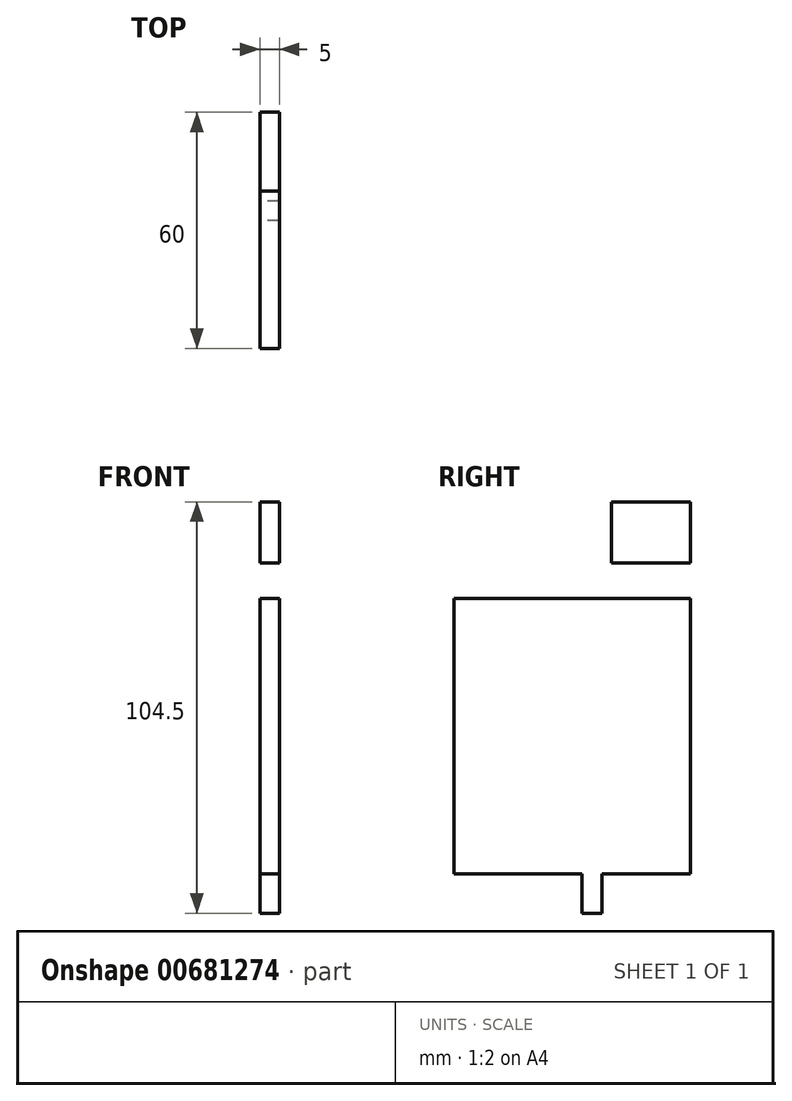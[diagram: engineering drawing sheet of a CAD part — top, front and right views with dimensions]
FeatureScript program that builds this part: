
annotation { "Feature Type Name" : "Feature", "Feature Type Description" : "" }
export const myFeature = defineFeature(function(context is Context, id is Id, definition is map)
    precondition{}
    {
        {
            var Q0;
            Q0=qCreatedBy(makeId("Right.planeOp"),FACE);
            var sketch = newSketch(context, id + "F0", { "sketchPlane" : qUnion([Q0])});
            skLineSegment(sketch, "E0", {"start": v(0, 0) * mm, "end": v(0, -70) * mm});
            skLineSegment(sketch, "E1", {"start": v(0, -70) * mm, "end": v(12.4, -70) * mm});
            skLineSegment(sketch, "E2.0", {"start": v(37.5, -70.04) * mm, "end": v(37.5, -81.07) * mm});
            skLineSegment(sketch, "E3", {"start": v(12, -70) * mm, "end": v(12.4, -70) * mm});
            skLineSegment(sketch, "E4", {"start": v(0, -70) * mm, "end": v(12, -70) * mm});
            skLineSegment(sketch, "E5", {"start": v(32.5, -80) * mm, "end": v(32.5, -70) * mm});
            skPoint(sketch, "E6.trimOffspring.start.orphan", {"position": v(25, -70) * mm});
            skLineSegment(sketch, "E7", {"start": v(37.5, -80) * mm, "end": v(37.5, -81.07) * mm});
            skLineSegment(sketch, "E8", {"start": v(32.5, -80) * mm, "end": v(37.5, -80) * mm});
            skLineSegment(sketch, "E9", {"start": v(11.37, -27.14) * mm, "end": v(11.37, -26.74) * mm});
            skLineSegment(sketch, "E10", {"start": v(38.63, -27.14) * mm, "end": v(38.63, -26.74) * mm});
            skLineSegment(sketch, "E11", {"start": v(0, -70) * mm, "end": v(32.5, -70) * mm});
            skLineSegment(sketch, "E12.trimOffspring", {"start": v(32.5, -70) * mm, "end": v(0, -70) * mm});
            skLineSegment(sketch, "E13", {"start": v(22.5, -0.04) * mm, "end": v(0, 0) * mm});
            skLineSegment(sketch, "E14.0", {"start": v(60, -0.04) * mm, "end": v(60, -70.04) * mm});
            skLineSegment(sketch, "E15", {"start": v(60, -0.04) * mm, "end": v(22.5, -0.04) * mm});
            skLineSegment(sketch, "E16", {"start": v(60, -70.04) * mm, "end": v(37.5, -70.04) * mm});
            skLineSegment(sketch, "E17.0", {"start": v(42.5, 9) * mm, "end": v(40, 9) * mm});
            skPoint(sketch, "E18.orphan", {"position": v(42.5, 0) * mm});
            skLineSegment(sketch, "E19", {"start": v(40, 24.5) * mm, "end": v(42.5, 24.5) * mm});
            skPoint(sketch, "E19.startSnap0", {"position": v(42.5, 24.5) * mm});
            skPoint(sketch, "E19.endSnap0", {"position": v(42.5, 24.5) * mm});
            skPoint(sketch, "E20.end.orphan", {"position": v(42.5, 40) * mm});
            skLineSegment(sketch, "E21", {"start": v(60, 9) * mm, "end": v(60, 24.5) * mm});
            skLineSegment(sketch, "E22", {"start": v(42.5, 24.5) * mm, "end": v(60, 24.5) * mm});
            skLineSegment(sketch, "E23", {"start": v(42.5, 9) * mm, "end": v(60, 9) * mm});
            skPoint(sketch, "E24.orphan", {"position": v(22.5, 24.5) * mm});
            skLineSegment(sketch, "E25.0", {"start": v(40, 9) * mm, "end": v(40, 24.5) * mm});
            skSolve(sketch);
        }
        {
            var Q0;
            {var subQ1=sQuery(id+"F0.wireOp",EDGE,"E0");Q0=makeQuery(id+"F0.imprint","IMPRINT",FACE,{"disambiguationData":[TD([[makeQuery(id+"F0.imprint","IMPRINT",EDGE,{"derivedFrom":subQ1}),1.0]])]});}
            var Q1;
            Q1=makeQuery(id+"F0.imprint","IMPRINT",FACE,{"disambiguationData":[TD([[makeQuery(id+"F0.imprint","IMPRINT",EDGE,{"derivedFrom":sQuery(id+"F0.wireOp",EDGE,"KUJi0EKv-68yc-6Nkf-644W-VpfIH1upkmh2")}),-1.0]])]});
            var Q2;
            Q2=makeQuery(id+"F0.imprint","IMPRINT",FACE,{"disambiguationData":[TD([[makeQuery(id+"F0.imprint","IMPRINT",EDGE,{"derivedFrom":sQuery(id+"F0.wireOp",EDGE,"E17.0")}),-1.0]])]});
            extrude(context, id + "F1", {"entities" : qUnion([Q0, Q1, Q2]), "depth" : 5 * mm, "offsetDistance" : 25 * mm});
        }
    });
